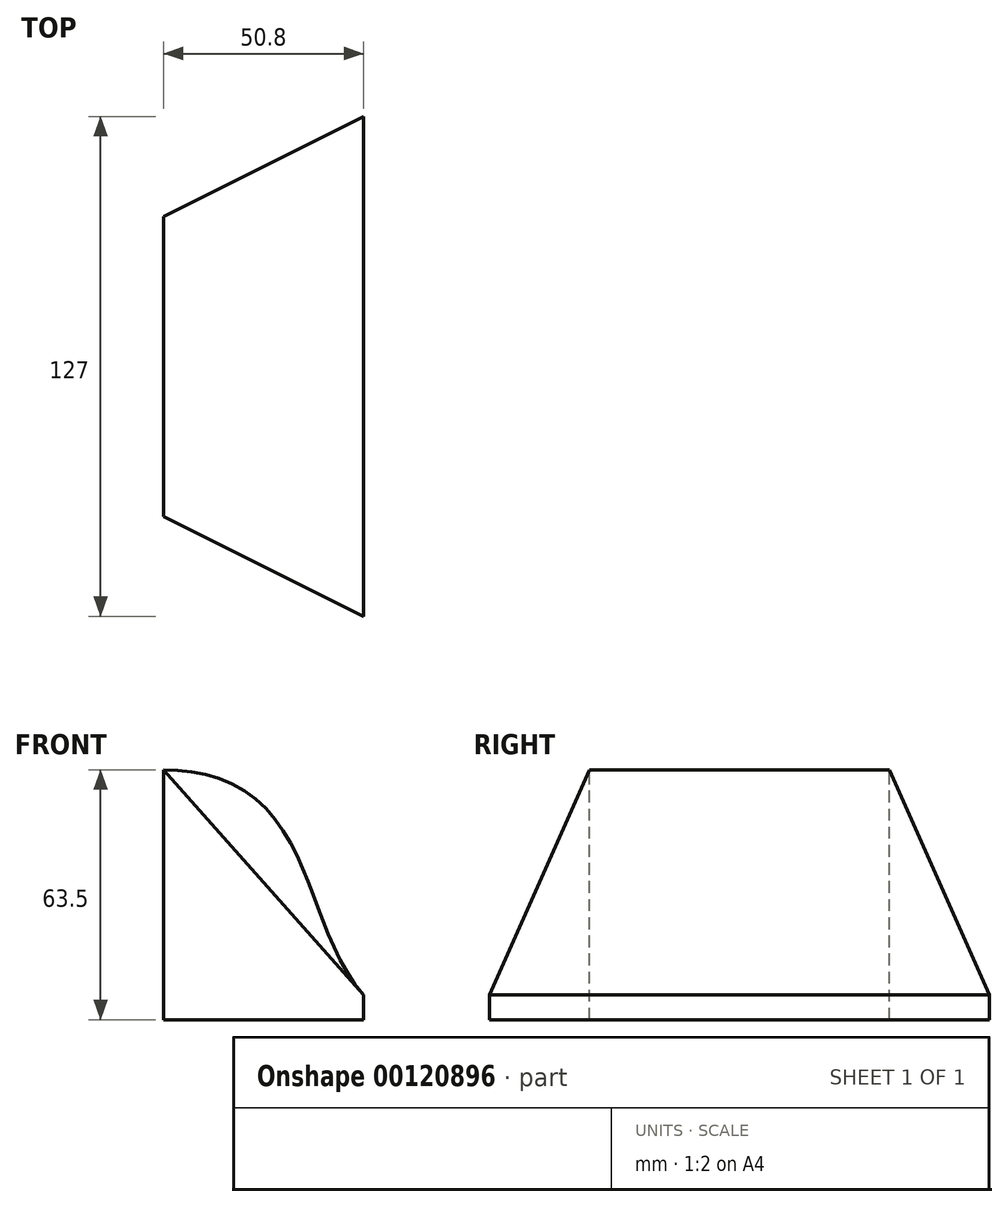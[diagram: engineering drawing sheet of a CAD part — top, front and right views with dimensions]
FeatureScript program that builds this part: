
annotation { "Feature Type Name" : "Feature", "Feature Type Description" : "" }
export const myFeature = defineFeature(function(context is Context, id is Id, definition is map)
    precondition{}
    {
        {
            var Q0;
            Q0=qCreatedBy(makeId("Right.planeOp"),FACE);
            var sketch = newSketch(context, id + "F0", { "sketchPlane" : qUnion([Q0])});
            skLineSegment(sketch, "E0.bottom", {"start": v(-38.1, 0) * mm, "end": v(38.1, 0) * mm});
            skLineSegment(sketch, "E0.top", {"start": v(-38.1, 63.5) * mm, "end": v(38.1, 63.5) * mm});
            skLineSegment(sketch, "E0.left", {"start": v(-38.1, 0) * mm, "end": v(-38.1, 63.5) * mm});
            skLineSegment(sketch, "E0.right", {"start": v(38.1, 0) * mm, "end": v(38.1, 63.5) * mm});
            skSolve(sketch);
        }
        {
            var Q0;
            Q0=qCreatedBy(makeId("Right.planeOp"),FACE);
            cPlane(context, id + "F1", {"entities" : qUnion([Q0]), "cplaneType" : CPlaneType.OFFSET, "offset" : 50.8 * mm, "width" : 152.4 * mm, "height" : 152.4 * mm});
        }
        {
            var Q0;
            Q0=qCreatedBy(id+"F1.planeOp",FACE);
            var sketch = newSketch(context, id + "F2", { "sketchPlane" : qUnion([Q0])});
            skLineSegment(sketch, "E1.0.1", {"start": v(-38.1, 0) * mm, "end": v(38.1, 0) * mm});
            skLineSegment(sketch, "E2", {"start": v(-38.1, 6.35) * mm, "end": v(38.1, 6.35) * mm});
            skLineSegment(sketch, "E3.bottom", {"start": v(-38.1, 6.35) * mm, "end": v(-63.5, 6.35) * mm});
            skLineSegment(sketch, "E3.top", {"start": v(-38.1, 0) * mm, "end": v(-63.5, 0) * mm});
            skLineSegment(sketch, "E3.right", {"start": v(-63.5, 6.35) * mm, "end": v(-63.5, 0) * mm});
            skLineSegment(sketch, "E4.bottom", {"start": v(38.1, 6.35) * mm, "end": v(63.5, 6.35) * mm});
            skLineSegment(sketch, "E4.top", {"start": v(38.1, 0) * mm, "end": v(63.5, 0) * mm});
            skLineSegment(sketch, "E4.right", {"start": v(63.5, 6.35) * mm, "end": v(63.5, 0) * mm});
            skSolve(sketch);
        }
        {
            var Q0;
            Q0=qCreatedBy(id+"F1.planeOp",FACE);
            var sketch = newSketch(context, id + "F3", { "sketchPlane" : qUnion([Q0])});
            skPoint(sketch, "E5.0", {"position": v(-63.5, 0) * mm});
            skPoint(sketch, "E6.0", {"position": v(63.5, 6.35) * mm});
            skLineSegment(sketch, "E7.bottom", {"start": v(-63.5, 0) * mm, "end": v(63.5, 0) * mm});
            skLineSegment(sketch, "E7.top", {"start": v(-63.5, 6.35) * mm, "end": v(63.5, 6.35) * mm});
            skLineSegment(sketch, "E7.left", {"start": v(-63.5, 0) * mm, "end": v(-63.5, 6.35) * mm});
            skLineSegment(sketch, "E7.right", {"start": v(63.5, 0) * mm, "end": v(63.5, 6.35) * mm});
            skSolve(sketch);
        }
        {
            var Q0;
            Q0=qCreatedBy(makeId("Front.planeOp"),FACE);
            var sketch = newSketch(context, id + "F4", { "sketchPlane" : qUnion([Q0])});
            skPoint(sketch, "E8.0", {"position": v(50.8, 6.35) * mm});
            skPoint(sketch, "E9", {"position": v(0, 63.5) * mm});
            skFitSpline(sketch, "E10", {"points": [v(0, 63.5) * mm, v(50.8, 6.35) * mm], "startDerivative": vector(117.41, -1) * mm, "endDerivative": vector(50.8, -57.15) * mm});
            skSolve(sketch);
        }
        {
            var Q0;
            Q0 = qSketchRegion(id + "F0", true);
            var Q1;
            Q1 = qSketchRegion(id + "F3", true);
            var Q2;
            Q2=sQuery(id+"F4.wireOp",EDGE,"E10");
            loft(context, id + "F5", {"addGuides" : true, "sheetProfilesArray" : [{ "sheetProfileEntities" : qUnion([Q0]) }, { "sheetProfileEntities" : qUnion([Q1]) }], "guidesArray" : [{ "guideEntities" : qUnion([Q2]), "guideDerivativeType" : LoftGuideDerivativeType.DEFAULT, "guideDerivativeMagnitude" : 1 }]});
        }
    });
